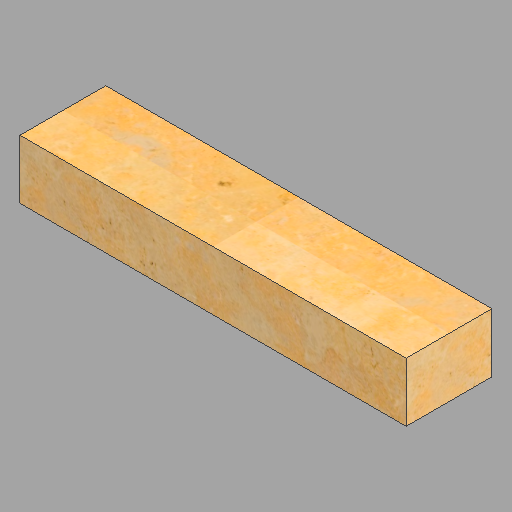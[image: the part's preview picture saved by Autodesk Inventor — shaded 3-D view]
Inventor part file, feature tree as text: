
AUTODESK INVENTOR PART (.ipt)
format: ipt  version: 2023 (Build 270158030, 158C)  size: 250,368 bytes
history: native  units: in
note: dims shown in document units (in); Inventor stores cm internally (conversion verified against a paired STEP export)
features: extrude x1, sketch x1
ambient origin geometry x8: Origin, YZ Plane, XZ Plane, XY Plane, X Axis, Y Axis, Z Axis, Center Point
bodies: Solid1 (feature_tree)
feature tree (2):
  extrude  "Extrusion1"  Depth=4.0in
  sketch  "Sketch1"  dims[d0=18.0in d1=4.0in d2=2.75in d3=0.0in]
